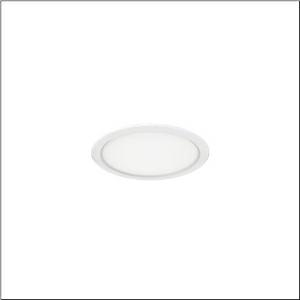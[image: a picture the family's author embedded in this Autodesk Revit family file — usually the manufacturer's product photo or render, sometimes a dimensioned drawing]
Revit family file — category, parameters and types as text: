
# Revit family: lunis_41_eco_51ds107d33b
name_source: partatom
category: Lighting Fixtures
units: mm (PartAtom-declared; Revit-internal decimal feet)

## family parameters
Cut with Voids When Loaded = No
Host = Face
Light Source = No
Part Type = Normal
Room Calculation Point = No
Round Connector Dimension = Use Diameter
Shared = No

## types (1)
- Lunis 41 Eco (1 x LED, 1460 lm, 12 W, 3000K)
    Apparent Load = 12 VA
    CIE Flux Codes = 47 80 97 100 100
    Color Rendering = 80
    Color Temperature = 3000K
    Default Elevation = 1800 mm
    Description = Lunis 41 Eco, downlight, light emission: direct distribution, LED rated luminous flux: 1.460lm, light colour: 830, mains connection: 230V, AC, 50/60Hz, housing, round, of aluminium, coated, traffic white (RAL 9016), diameter: 166mm, recess depth: 54mm, protection rating (complete): IP20, protection rating (on room side): IP40, insulation class (complete): insulation class II (safety insulation), certification: CE, permissible ambient temperature for indoor applications: -20..+40°C, packaging unit: 1 piece
    Height = 0 mm  [stored 0 ft]
    Lamp = 1 x LED
    Lamp Light Flux = 1460 lm
    Lamp Power = 12 W
    Lamp count = 1
    Length = 166 mm
    Luminous efficacy = 122 lm/W
    Manufacturer = Siteco
    ModVariant = No
    Model = 51DS107D33B
    Mounting Place = Ceiling
    Mounting Type = Recessed
    Number of Poles = 1
    OnlyDefault = Yes
    Power Factor = 1
    Product Name = Lunis 41 Eco
    Product group = downlight
    ProductGroupID = 401
    Protection Class = Protection class II
    Protection Degree = IP 20
    RLX_Detail_Level = 1
    RLX_Emergency_Light_Flux = 0 lm
    RLX_Emergency_Type = 0
    RLX_Emergency_Type_DB = No
    RlxData = <blob elided: 8893 chars, md5=fd09502a>
    Socket = socket
    Standby Power = 0 W
    System Light Flux = 1460 lm
    System Power = 12 W
    Type Comments = Product without accessories
    Type Image = l_1345912.jpg
    URL = http://relux.com
    VarID = ---
    Voltage = 0 V
    Weight = 0.00 kg
    Width = 0 mm  [stored 0 ft]

note: [stored X ft] marks values corroborated as IEEE doubles in the binary element streams (Revit-internal decimal feet)

## geometry (parser evidence)
native form markers: Sweep x12
no freeform markers — native parametric forms only
